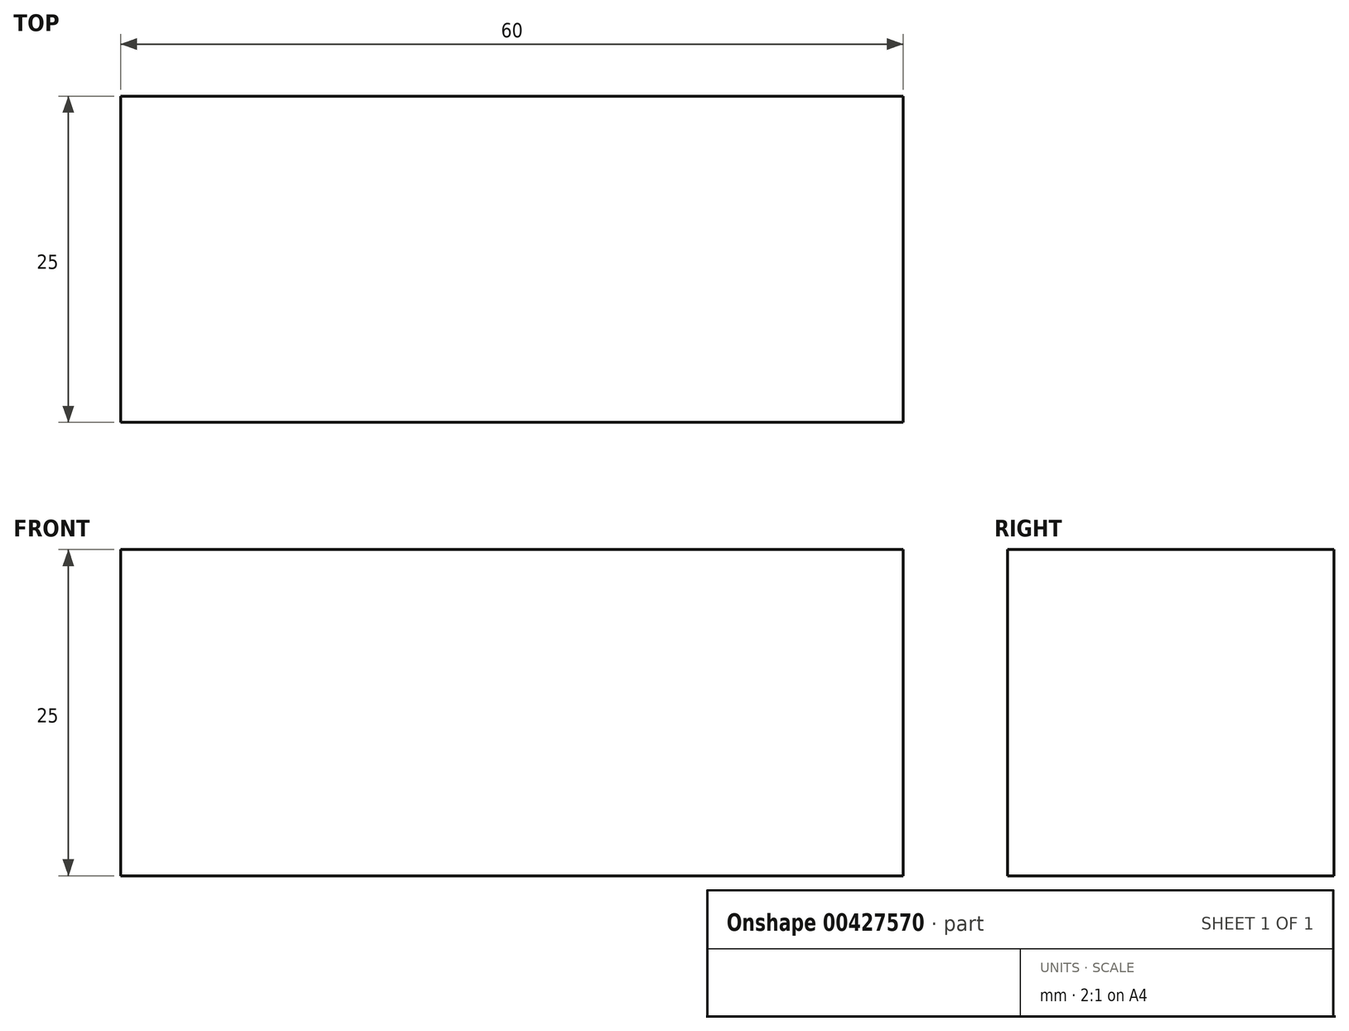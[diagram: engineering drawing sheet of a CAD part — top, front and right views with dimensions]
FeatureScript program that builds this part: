
annotation { "Feature Type Name" : "Feature", "Feature Type Description" : "" }
export const myFeature = defineFeature(function(context is Context, id is Id, definition is map)
    precondition{}
    {
        {
            var Q0;
            Q0=qCreatedBy(makeId("Top.planeOp"),FACE);
            var sketch = newSketch(context, id + "F0", { "sketchPlane" : qUnion([Q0])});
            skLineSegment(sketch, "E0.bottom", {"start": v(-68.38, -51.18) * mm, "end": v(-38.38, -51.18) * mm});
            skLineSegment(sketch, "E0.top", {"start": v(-68.38, -26.18) * mm, "end": v(-38.38, -26.18) * mm});
            skLineSegment(sketch, "E0.left", {"start": v(-68.38, -51.18) * mm, "end": v(-68.38, -26.18) * mm});
            skLineSegment(sketch, "E0.right", {"start": v(-38.38, -51.18) * mm, "end": v(-38.38, -26.18) * mm});
            skLineSegment(sketch, "E1.bottom", {"start": v(-38.38, -51.18) * mm, "end": v(-8.38, -51.18) * mm});
            skLineSegment(sketch, "E1.top", {"start": v(-38.38, -26.18) * mm, "end": v(-8.38, -26.18) * mm});
            skLineSegment(sketch, "E1.right", {"start": v(-8.38, -51.18) * mm, "end": v(-8.38, -26.18) * mm});
            skLineSegment(sketch, "E2.bottom", {"start": v(-8.38, -51.18) * mm, "end": v(-38.38, -51.18) * mm});
            skLineSegment(sketch, "E2.top", {"start": v(-8.38, -76.18) * mm, "end": v(-38.38, -76.18) * mm});
            skLineSegment(sketch, "E2.left", {"start": v(-8.38, -51.18) * mm, "end": v(-8.38, -76.18) * mm});
            skLineSegment(sketch, "E2.right", {"start": v(-38.38, -51.18) * mm, "end": v(-38.38, -76.18) * mm});
            skSolve(sketch);
        }
        {
            var Q0;
            Q0=makeQuery(id+"F0.imprint","IMPRINT",FACE,{"disambiguationData":[TD([[makeQuery(id+"F0.imprint","IMPRINT",EDGE,{"derivedFrom":sQuery(id+"F0.wireOp",EDGE,"E0.bottom")}),1.0]])]});
            var Q1;
            Q1=makeQuery(id+"F0.imprint","IMPRINT",FACE,{"disambiguationData":[TD([[makeQuery(id+"F0.imprint","IMPRINT",EDGE,{"derivedFrom":sQuery(id+"F0.wireOp",EDGE,"E1.top")}),-1.0]])]});
            var Q2;
            Q2=makeQuery(id+"F0.imprint","IMPRINT",FACE,{"disambiguationData":[TD([[makeQuery(id+"F0.imprint","IMPRINT",EDGE,{"derivedFrom":sQuery(id+"F0.wireOp",EDGE,"E2.bottom")}),1.0]])]});
            extrude(context, id + "F1", {"entities" : qUnion([Q0, Q1, Q2]), "depth" : 25 * mm});
        }
    });
